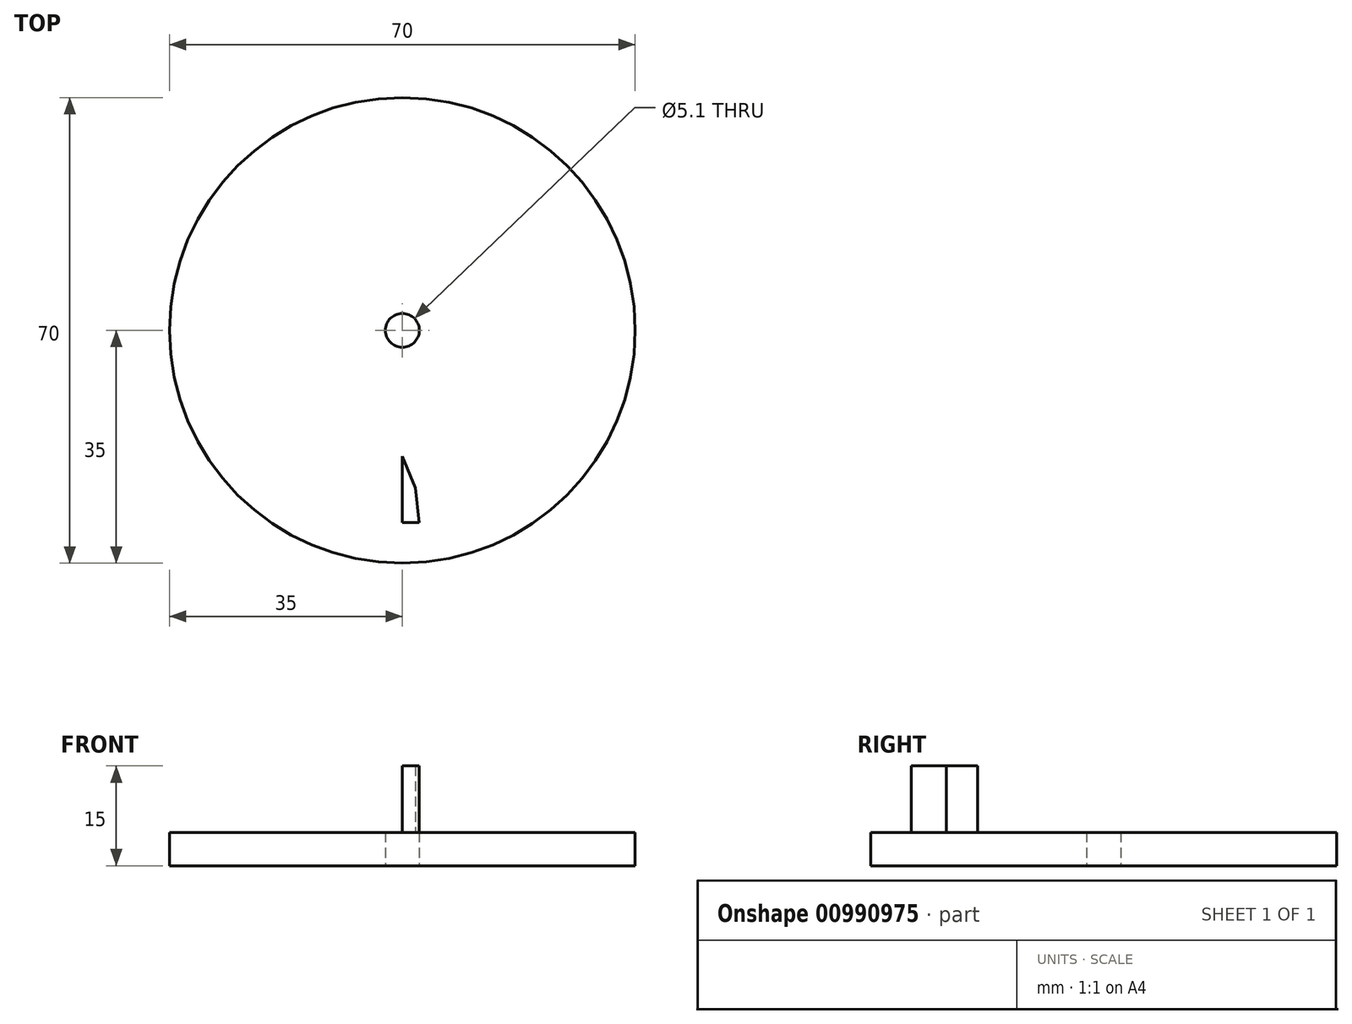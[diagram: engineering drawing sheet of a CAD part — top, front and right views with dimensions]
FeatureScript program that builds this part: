
annotation { "Feature Type Name" : "Feature", "Feature Type Description" : "" }
export const myFeature = defineFeature(function(context is Context, id is Id, definition is map)
    precondition{}
    {
        {
            var Q0;
            Q0=qCreatedBy(makeId("Top.planeOp"),FACE);
            var sketch = newSketch(context, id + "F0", { "sketchPlane" : qUnion([Q0])});
            skCircle(sketch, "E0", {"center": v(0, 0) * mm, "radius": 35 * mm});
            skCircle(sketch, "E1", {"center": v(0, 0) * mm, "radius": 2.55 * mm});
            skLineSegment(sketch, "E2", {"start": v(0, 0) * mm, "end": v(3.68, -34.8) * mm, "construction": true});
            skLineSegment(sketch, "E3", {"start": v(0, 0) * mm, "end": v(0, -35) * mm, "construction": true});
            skSolve(sketch);
        }
        {
            var Q0;
            Q0=makeQuery(id+"F0.imprint","IMPRINT",FACE,{"disambiguationData":[TD([[makeQuery(id+"F0.imprint","IMPRINT",EDGE,{"derivedFrom":sQuery(id+"F0.wireOp",EDGE,"E0")}),1.0]])]});
            extrude(context, id + "F1", {"entities" : qUnion([Q0]), "depth" : 5 * mm, "offsetDistance" : 25 * mm});
        }
        {
            var Q0;
            Q0=makeQuery(id+"F1.opExtrude","CAP_FACE",FACE,{"disambiguationData":[OSD([sQuery(id+"F0.wireOp",EDGE,"E0"),sQuery(id+"F0.wireOp",EDGE,"E1")])],"isStart":false});
            var sketch = newSketch(context, id + "F2", { "sketchPlane" : qUnion([Q0])});
            skLineSegment(sketch, "E4", {"start": v(0, -18.93) * mm, "end": v(0, -28.93) * mm});
            skLineSegment(sketch, "E5", {"start": v(0, -28.93) * mm, "end": v(2.5, -28.93) * mm});
            skLineSegment(sketch, "E6", {"start": v(2.5, -28.93) * mm, "end": v(1.94, -23.67) * mm});
            skLineSegment(sketch, "E7", {"start": v(1.94, -23.67) * mm, "end": v(0, -18.93) * mm});
            skSolve(sketch);
        }
        {
            var Q0;
            Q0=makeQuery(id+"F2.imprint","IMPRINT",FACE,{"disambiguationData":[TD([[makeQuery(id+"F2.imprint","IMPRINT",EDGE,{"derivedFrom":sQuery(id+"F2.wireOp",EDGE,"E4")}),1.0]])]});
            extrude(context, id + "F3", {"entities" : qUnion([Q0]), "operationType" : NewBodyOperationType.ADD, "depth" : 10 * mm, "offsetDistance" : 25 * mm});
        }
    });
